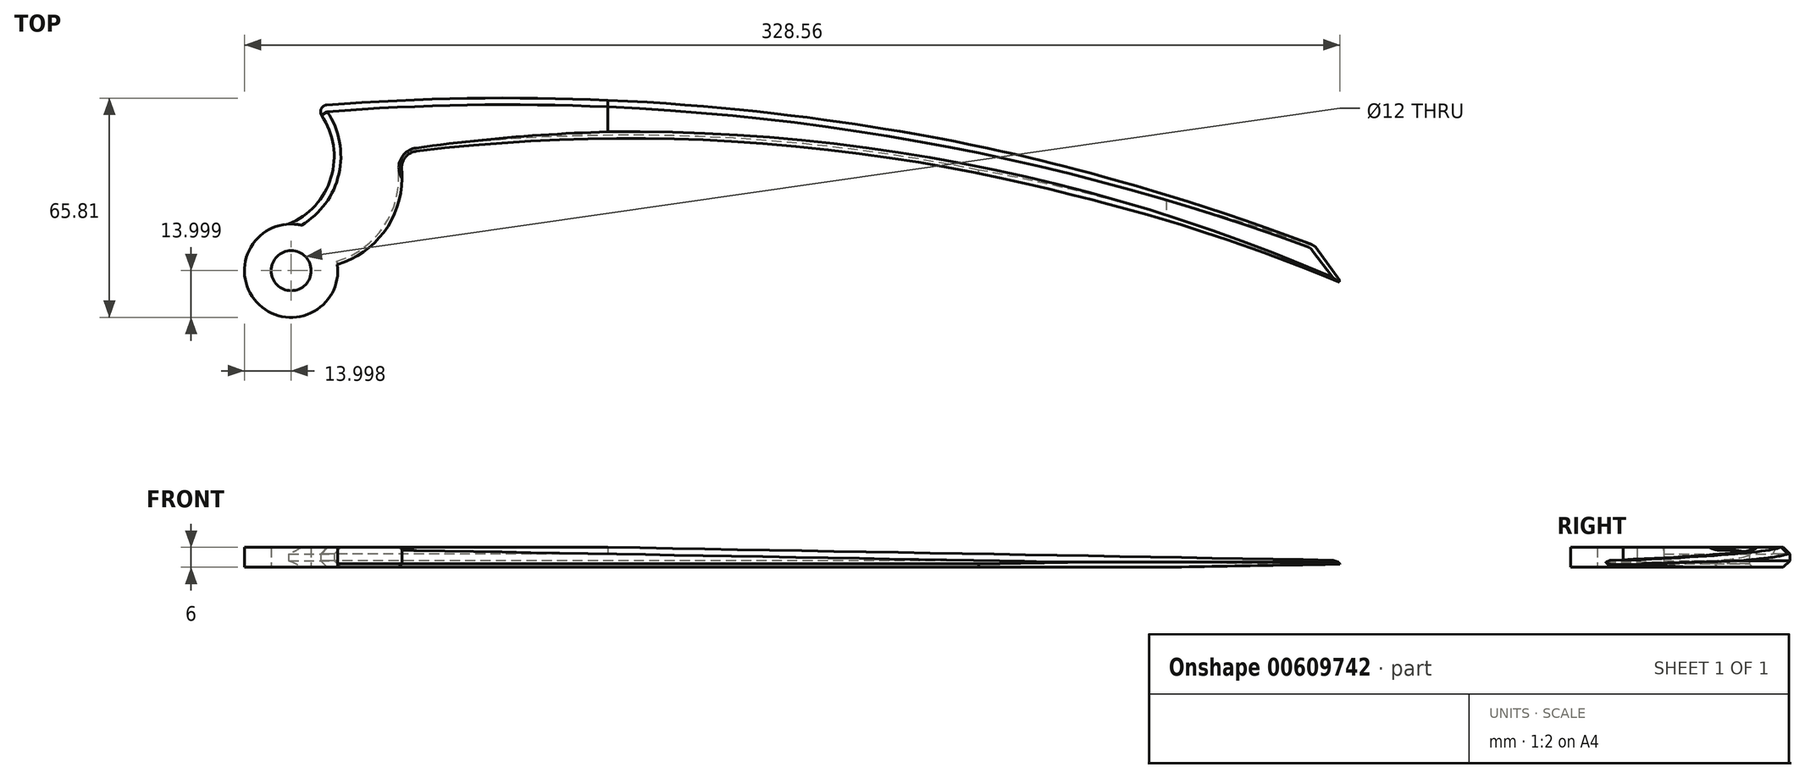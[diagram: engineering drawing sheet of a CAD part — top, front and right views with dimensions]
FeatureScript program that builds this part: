
annotation { "Feature Type Name" : "Feature", "Feature Type Description" : "" }
export const myFeature = defineFeature(function(context is Context, id is Id, definition is map)
    precondition{}
    {
        {
            var Q0;
            Q0=qCreatedBy(makeId("Top.planeOp"),FACE);
            var sketch = newSketch(context, id + "F0", { "sketchPlane" : qUnion([Q0])});
            skCircle(sketch, "E0", {"center": v(-118.82, 19.04) * mm, "radius": 14 * mm});
            skArc(sketch, "E1", {"start": v(-119.55, 33.02) * mm, "mid": v(-106.86, 47) * mm, "end": v(-109.66, 65.66) * mm});
            skArc(sketch, "E2", {"start": v(186.71, 28.1) * mm, "mid": v(41.46, 64.29) * mm, "end": v(-108.16, 68.77) * mm});
            skArc(sketch, "E3", {"start": v(-104.94, 20.87) * mm, "mid": v(-90.2, 31.74) * mm, "end": v(-85.66, 49.48) * mm});
            skLineSegment(sketch, "E4", {"start": v(188.98, 26.43) * mm, "end": v(199.85, 12.08) * mm});
            skArc(sketch, "E5", {"start": v(199.85, 12.08) * mm, "mid": v(62.2, 52.7) * mm, "end": v(-81.29, 54.9) * mm});
            skPoint(sketch, "E6.visualSharp", {"position": v(-86.53, 54.24) * mm});
            skArc(sketch, "E6.filletArc", {"start": v(-81.29, 54.9) * mm, "mid": v(-84.57, 53.08) * mm, "end": v(-85.66, 49.48) * mm});
            skPoint(sketch, "E7.visualSharp", {"position": v(-111.9, 68.47) * mm});
            skArc(sketch, "E7.filletArc", {"start": v(-108.16, 68.77) * mm, "mid": v(-109.8, 67.65) * mm, "end": v(-109.66, 65.66) * mm});
            skPoint(sketch, "E8.visualSharp", {"position": v(188.1, 27.6) * mm});
            skArc(sketch, "E8.filletArc", {"start": v(188.98, 26.43) * mm, "mid": v(187.96, 27.43) * mm, "end": v(186.71, 28.1) * mm});
            skCircle(sketch, "E9", {"center": v(-118.82, 19.04) * mm, "radius": 6 * mm});
            skSolve(sketch);
        }
        {
            var Q0;
            Q0=qSketchRegion(id+"F0",true);
            extrude(context, id + "F1", {"entities" : qUnion([Q0]), "depth" : 6 * mm, "offsetDistance" : 25 * mm});
        }
        {
            var Q0;
            Q0=qCreatedBy(makeId("Front.planeOp"),FACE);
            var sketch = newSketch(context, id + "F2", { "sketchPlane" : qUnion([Q0])});
            skLineSegment(sketch, "E10", {"start": v(227.38, 1.5) * mm, "end": v(-107.62, -4.5) * mm});
            skLineSegment(sketch, "E11", {"start": v(-107.62, -4.5) * mm, "end": v(262.38, -4.5) * mm});
            skLineSegment(sketch, "E12", {"start": v(262.38, -4.5) * mm, "end": v(262.38, 7.5) * mm});
            skLineSegment(sketch, "E13", {"start": v(227.38, 1.5) * mm, "end": v(-107.62, 7.5) * mm});
            skLineSegment(sketch, "E14", {"start": v(-107.62, 7.5) * mm, "end": v(262.38, 7.5) * mm});
            skSolve(sketch);
        }
        {
            var Q0;
            Q0=qSketchRegion(id+"F2",true);
            extrude(context, id + "F3", {"entities" : qUnion([Q0]), "operationType" : NewBodyOperationType.REMOVE, "oppositeDirection" : true, "depth" : 111 * mm, "offsetDistance" : 25 * mm});
        }
        {
            var Q0;
            Q0=makeQuery(id+"F1.opExtrude","CAP_EDGE",EDGE,{"disambiguationData":[OSD([sQuery(id+"F0.wireOp",EDGE,"E2")])],"isStart":true});
            var Q1;
            Q1=makeQuery(id+"F1.opExtrude","CAP_EDGE",EDGE,{"disambiguationData":[OSD([sQuery(id+"F0.wireOp",EDGE,"E2")])],"isStart":false});
            chamfer(context, id + "F4", {"entities" : qUnion([Q0, Q1]), "width" : 2 * mm, "tangentPropagation" : true});
        }
        {
            var Q0;
            Q0=makeQuery(id+"F3.boolean.opBoolean","INTERSECT",EDGE,{"derivedFrom":[makeQuery(id+"F1.opExtrude","SWEPT_FACE",FACE,{"disambiguationData":[OSD([sQuery(id+"F0.wireOp",EDGE,"E2")])]}),makeQuery(id+"F3.opExtrude","SWEPT_FACE",FACE,{"disambiguationData":[OSD([sQuery(id+"F2.wireOp",EDGE,"E10")])]})]});
            var Q1;
            Q1=makeQuery(id+"F3.boolean.opBoolean","INTERSECT",EDGE,{"derivedFrom":[makeQuery(id+"F1.opExtrude","SWEPT_FACE",FACE,{"disambiguationData":[OSD([sQuery(id+"F0.wireOp",EDGE,"E2")])]}),makeQuery(id+"F3.opExtrude","SWEPT_FACE",FACE,{"disambiguationData":[OSD([sQuery(id+"F2.wireOp",EDGE,"E13")])]})]});
            chamfer(context, id + "F5", {"entities" : qUnion([Q0, Q1]), "width" : 2 * mm, "tangentPropagation" : true});
        }
        {
            var Q0;
            Q0=makeQuery(id+"F3.boolean.opBoolean","INTERSECT",EDGE,{"derivedFrom":[makeQuery(id+"F1.opExtrude","SWEPT_FACE",FACE,{"disambiguationData":[OSD([sQuery(id+"F0.wireOp",EDGE,"E5")])]}),makeQuery(id+"F3.opExtrude","SWEPT_FACE",FACE,{"disambiguationData":[OSD([sQuery(id+"F2.wireOp",EDGE,"E10")])]})]});
            var Q1;
            Q1=makeQuery(id+"F3.boolean.opBoolean","INTERSECT",EDGE,{"derivedFrom":[makeQuery(id+"F1.opExtrude","SWEPT_FACE",FACE,{"disambiguationData":[OSD([sQuery(id+"F0.wireOp",EDGE,"E5")])]}),makeQuery(id+"F3.opExtrude","SWEPT_FACE",FACE,{"disambiguationData":[OSD([sQuery(id+"F2.wireOp",EDGE,"E13")])]})]});
            chamfer(context, id + "F6", {"entities" : qUnion([Q0, Q1]), "width" : 2 * mm, "tangentPropagation" : true});
        }
        {
            var Q0;
            Q0=makeQuery(id+"F1.opExtrude","CAP_EDGE",EDGE,{"disambiguationData":[OSD([sQuery(id+"F0.wireOp",EDGE,"E5")])],"isStart":true});
            var Q1;
            Q1=makeQuery(id+"F1.opExtrude","CAP_EDGE",EDGE,{"disambiguationData":[OSD([sQuery(id+"F0.wireOp",EDGE,"E5")])],"isStart":false});
            chamfer(context, id + "F7", {"entities" : qUnion([Q0, Q1]), "width" : 1 * mm, "tangentPropagation" : true});
        }
    });
